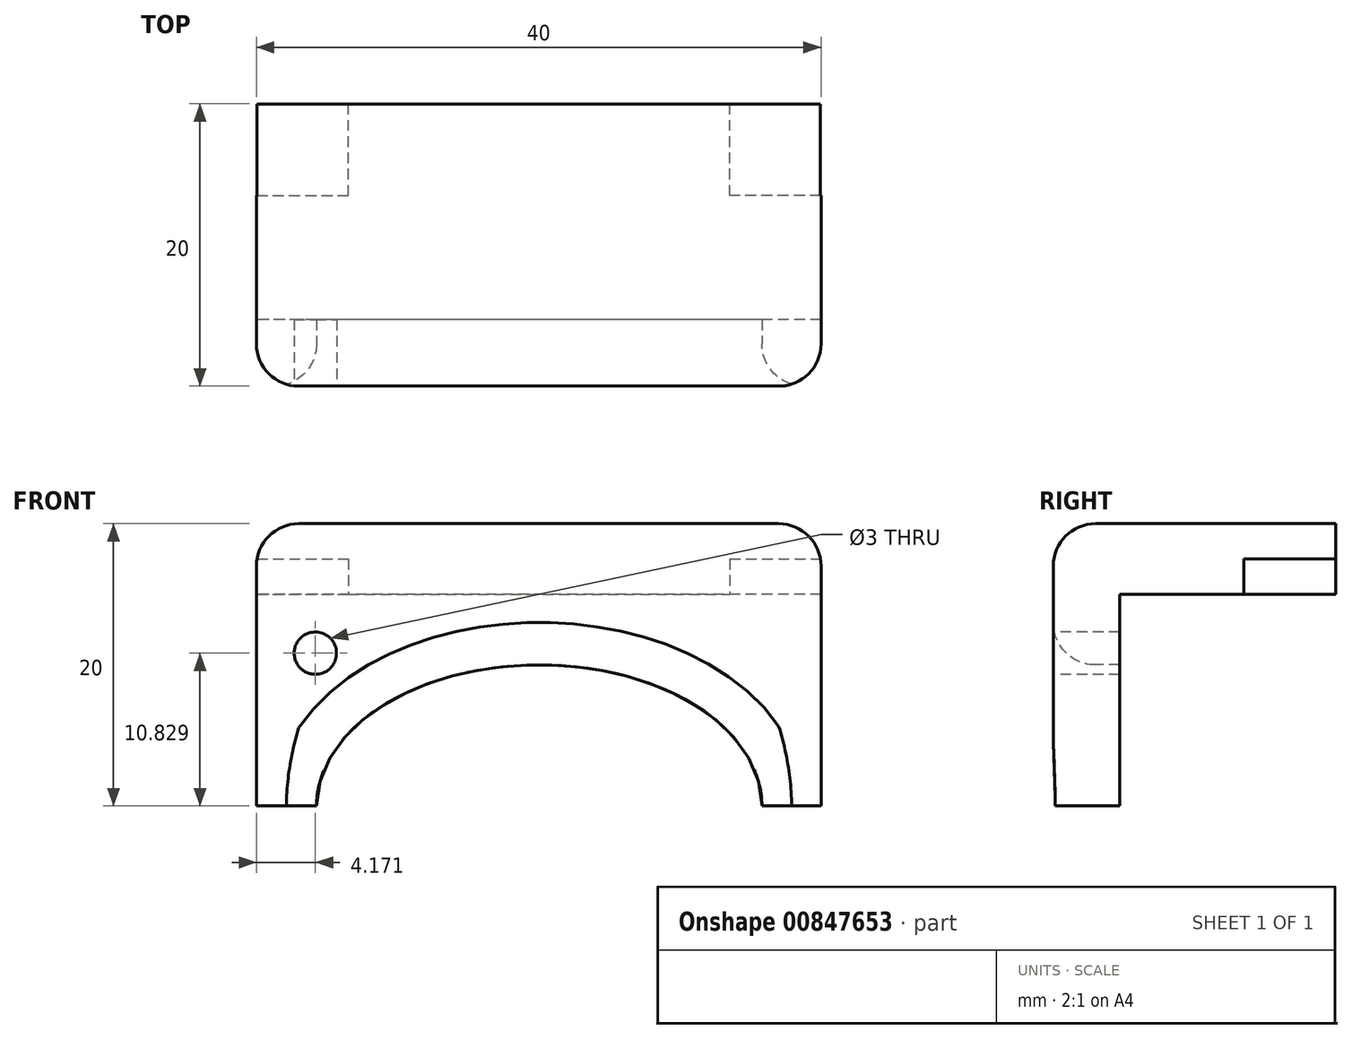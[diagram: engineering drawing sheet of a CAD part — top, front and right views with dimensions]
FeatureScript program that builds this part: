
annotation { "Feature Type Name" : "Feature", "Feature Type Description" : "" }
export const myFeature = defineFeature(function(context is Context, id is Id, definition is map)
    precondition{}
    {
        {
            var Q0;
            Q0=qCreatedBy(makeId("Right.planeOp"),FACE);
            var sketch = newSketch(context, id + "F0", { "sketchPlane" : qUnion([Q0])});
            skLineSegment(sketch, "E0", {"start": v(-4.59, 5) * mm, "end": v(-4.59, 20) * mm});
            skLineSegment(sketch, "E1", {"start": v(-4.59, 20) * mm, "end": v(10.7, 20) * mm});
            skLineSegment(sketch, "E2", {"start": v(10.7, 20) * mm, "end": v(10.7, 25) * mm});
            skLineSegment(sketch, "E3", {"start": v(10.7, 25) * mm, "end": v(-9.3, 25) * mm});
            skLineSegment(sketch, "E4", {"start": v(-9.3, 25) * mm, "end": v(-9.3, 5) * mm});
            skLineSegment(sketch, "E5", {"start": v(-9.3, 5) * mm, "end": v(-4.59, 5) * mm});
            skLineSegment(sketch, "E6", {"start": v(10.7, 22.5) * mm, "end": v(-4.62, 22.5) * mm, "construction": true});
            skSolve(sketch);
        }
        {
            var Q0;
            Q0=makeQuery(id+"F0.imprint","IMPRINT",FACE,{"disambiguationData":[TD([[makeQuery(id+"F0.imprint","IMPRINT",EDGE,{"derivedFrom":sQuery(id+"F0.wireOp",EDGE,"E0")}),1.0]])]});
            extrude(context, id + "F1", {"entities" : qUnion([Q0]), "depth" : 40 * mm, "offsetDistance" : 25 * mm});
        }
        {
            var Q0;
            Q0=qCreatedBy(makeId("Top.planeOp"),FACE);
            var sketch = newSketch(context, id + "F2", { "sketchPlane" : qUnion([Q0])});
            skLineSegment(sketch, "E7", {"start": v(0, 4.2) * mm, "end": v(6.5, 4.2) * mm});
            skLineSegment(sketch, "E8", {"start": v(6.5, 4.2) * mm, "end": v(6.5, 10.7) * mm});
            skLineSegment(sketch, "E9", {"start": v(0, 10.7) * mm, "end": v(40.08, -9.39) * mm, "construction": true});
            skLineSegment(sketch, "E10", {"start": v(0, -9.39) * mm, "end": v(39.98, 10.7) * mm, "construction": true});
            skLineSegment(sketch, "E11", {"start": v(39.98, 10.7) * mm, "end": v(20.02, 0.67) * mm, "construction": true});
            skLineSegment(sketch, "E12", {"start": v(20.02, 0.67) * mm, "end": v(20.02, 10.7) * mm, "construction": true});
            skLineSegment(sketch, "E13.MirrorCS", {"start": v(33.53, 4.2) * mm, "end": v(33.53, 10.7) * mm});
            skLineSegment(sketch, "E14.MirrorCS", {"start": v(40.03, 4.2) * mm, "end": v(33.53, 4.2) * mm});
            skLineSegment(sketch, "E15", {"start": v(0, 4.2) * mm, "end": v(0, 10.7) * mm});
            skLineSegment(sketch, "E16.MirrorCS", {"start": v(40.03, 4.2) * mm, "end": v(40.03, 10.7) * mm});
            skLineSegment(sketch, "E17", {"start": v(0, 10.7) * mm, "end": v(6.5, 10.7) * mm});
            skLineSegment(sketch, "E18.MirrorCS", {"start": v(40.03, 10.7) * mm, "end": v(33.53, 10.7) * mm});
            skSolve(sketch);
        }
        {
            var Q0;
            Q0=makeQuery(id+"F2.imprint","IMPRINT",FACE,{"disambiguationData":[TD([[makeQuery(id+"F2.imprint","IMPRINT",EDGE,{"derivedFrom":sQuery(id+"F2.wireOp",EDGE,"E13.MirrorCS")}),-1.0]])]});
            var Q1;
            Q1=makeQuery(id+"F2.imprint","IMPRINT",FACE,{"disambiguationData":[TD([[makeQuery(id+"F2.imprint","IMPRINT",EDGE,{"derivedFrom":sQuery(id+"F2.wireOp",EDGE,"E7")}),1.0]])]});
            var Q2;
            Q2=makeQuery(id+"F1.opExtrude","SWEPT_FACE",FACE,{"disambiguationData":[OSD([sQuery(id+"F0.wireOp",EDGE,"E1")])]});
            var Q3;
            Q3=makeQuery(id+"F1.opExtrude","SWEPT_BODY",BODY,{"disambiguationData":[OSD([sQuery(id+"F0.wireOp",EDGE,"E0"),sQuery(id+"F0.wireOp",EDGE,"E1"),sQuery(id+"F0.wireOp",EDGE,"E2"),sQuery(id+"F0.wireOp",EDGE,"E3"),sQuery(id+"F0.wireOp",EDGE,"E4"),sQuery(id+"F0.wireOp",EDGE,"E5")])]});
            var Q4;
            Q4=qCreatedBy(makeId("Front.planeOp"),FACE);
            extrude(context, id + "F3", {"entities" : qUnion([Q0, Q1]), "operationType" : NewBodyOperationType.REMOVE, "depth" : 22.5 * mm, "endBoundEntityFace" : qUnion([Q2]), "endBoundEntityBody" : qUnion([Q3]), "offsetDistance" : 25 * mm, "hasSecondDirection" : true, "secondDirectionOppositeDirection" : false, "secondDirectionDepth" : 20 * mm, "secondDirectionBoundEntityFace" : qUnion([Q4])});
        }
        {
            var Q0;
            Q0=makeQuery(id+"F1.opExtrude","SWEPT_FACE",FACE,{"disambiguationData":[OSD([sQuery(id+"F0.wireOp",EDGE,"E4")])]});
            cPlane(context, id + "F4", {"entities" : qUnion([Q0]), "cplaneType" : CPlaneType.OFFSET, "offset" : 5 * mm, "width" : 150 * mm, "height" : 150 * mm});
        }
        {
            var Q0;
            Q0=qCreatedBy(id+"F4.planeOp",FACE);
            var sketch = newSketch(context, id + "F5", { "sketchPlane" : qUnion([Q0])});
            skLineSegment(sketch, "E19", {"start": v(0, 25) * mm, "end": v(39.94, 4.98) * mm, "construction": true});
            skLineSegment(sketch, "E20", {"start": v(0, 5) * mm, "end": v(40, 24.96) * mm, "construction": true});
            skLineSegment(sketch, "E21", {"start": v(4.17, 31.45) * mm, "end": v(4.17, 1) * mm, "construction": true});
            skLineSegment(sketch, "E22", {"start": v(0, 20) * mm, "end": v(40.06, 20) * mm, "construction": true});
            skLineSegment(sketch, "E23", {"start": v(0, 15.83) * mm, "end": v(38.81, 15.83) * mm, "construction": true});
            skCircle(sketch, "E24", {"center": v(4.17, 15.83) * mm, "radius": 1.5 * mm});
            skLineSegment(sketch, "E25", {"start": v(20.03, 15) * mm, "end": v(20.03, 27.72) * mm, "construction": true});
            skPoint(sketch, "E25.startSnap0", {"position": v(20.03, 20) * mm});
            skCircle(sketch, "E26.MirrorC", {"center": v(35.9, 15.83) * mm, "radius": 1.5 * mm});
            skLineSegment(sketch, "E27", {"start": v(20.03, 27.07) * mm, "end": v(20.03, -1.03) * mm, "construction": true});
            skLineSegment(sketch, "E28", {"start": v(0, 5) * mm, "end": v(39.94, 4.98) * mm, "construction": true});
            skEllipticalArc(sketch, "E29", {});
            skLineSegment(sketch, "E30", {"start": v(4.17, 5) * mm, "end": v(35.81, 4.98) * mm});
            const initialGuessF5  = {"E29": [0.020031826570630074, 0.004989486402756663, -1, 0, 0.015778187662363052, 0.010008591224532622, 3.140765254858719, 6.282357908448509]};
            skSetInitialGuess(sketch, initialGuessF5);
            skSolve(sketch);
        }
        {
            var Q0;
            Q0=makeQuery(id+"F5.imprint","IMPRINT",FACE,{"disambiguationData":[TD([[makeQuery(id+"F5.imprint","IMPRINT",EDGE,{"derivedFrom":sQuery(id+"F5.wireOp",EDGE,"E24")}),1.0]])]});
            var Q1;
            Q1=makeQuery(id+"F5.imprint","IMPRINT",FACE,{"disambiguationData":[TD([[makeQuery(id+"F5.imprint","IMPRINT",EDGE,{"derivedFrom":sQuery(id+"F5.wireOp",EDGE,"E26.MirrorC")}),-1.0]])]});
            var Q2;
            {var subQ0=sQuery(id+"F5.wireOp",EDGE,"E29");Q2=makeQuery(id+"F5.imprint","IMPRINT",FACE,{"disambiguationData":[TD([[makeQuery(id+"F5.imprint","IMPRINT",EDGE,{"derivedFrom":subQ0}),1.0]])]});}
            var Q3;
            Q3=sQuery(id+"F5.wireOp",EDGE,"E24");
            var Q4;
            Q4=sQuery(id+"F5.wireOp",EDGE,"E26.MirrorC");
            extrude(context, id + "F6", {"entities" : qUnion([Q0, Q1, Q2]), "operationType" : NewBodyOperationType.REMOVE, "surfaceEntities" : qUnion([Q3, Q4]), "endBound" : BoundingType.THROUGH_ALL, "oppositeDirection" : true, "depth" : 25 * mm, "offsetDistance" : 25 * mm});
        }
        {
            var Q0;
            Q0=makeQuery(id+"F1.opExtrude","CAP_EDGE",EDGE,{"disambiguationData":[OSD([sQuery(id+"F0.wireOp",EDGE,"E3")])],"isStart":true});
            var Q1;
            Q1=makeQuery(id+"F1.opExtrude","CAP_EDGE",EDGE,{"disambiguationData":[OSD([sQuery(id+"F0.wireOp",EDGE,"E4")])],"isStart":true});
            var Q2;
            Q2=makeQuery(id+"F1.opExtrude","SWEPT_EDGE",EDGE,{"disambiguationData":[OSD([sQuery(id+"F0.wireOp",EDGE,"E3"),sQuery(id+"F0.wireOp",EDGE,"E4")])]});
            var Q3;
            Q3=makeQuery(id+"F1.opExtrude","CAP_EDGE",EDGE,{"disambiguationData":[OSD([sQuery(id+"F0.wireOp",EDGE,"E3")])],"isStart":false});
            var Q4;
            Q4=makeQuery(id+"F1.opExtrude","CAP_EDGE",EDGE,{"disambiguationData":[OSD([sQuery(id+"F0.wireOp",EDGE,"E4")])],"isStart":false});
            var Q5;
            Q5=makeQuery(id+"F1.opExtrude","SWEPT_EDGE",EDGE,{"disambiguationData":[OSD([sQuery(id+"F0.wireOp",EDGE,"E4"),sQuery(id+"F0.wireOp",EDGE,"E5")])]});
            var Q6;
            Q6=makeQuery(id+"F6.boolean.opBoolean","INTERSECT",EDGE,{"derivedFrom":[makeQuery(id+"F1.opExtrude","SWEPT_FACE",FACE,{"disambiguationData":[OSD([sQuery(id+"F0.wireOp",EDGE,"E4")])]}),makeQuery(id+"F6.opExtrude","SWEPT_FACE",FACE,{"disambiguationData":[OSD([sQuery(id+"F5.wireOp",EDGE,"E29")])]})]});
            fillet(context, id + "F7", {"entities" : qUnion([Q0, Q1, Q2, Q3, Q4, Q5, Q6]), "radius" : 3 * mm, "tangentPropagation" : true, "allowEdgeOverflow" : false});
        }
    });
